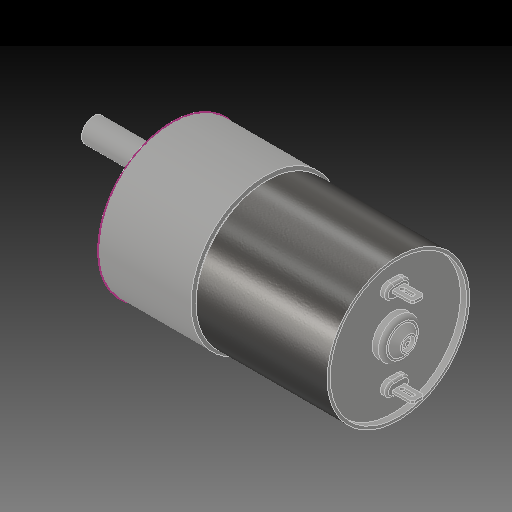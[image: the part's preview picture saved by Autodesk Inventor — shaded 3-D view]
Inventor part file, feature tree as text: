
AUTODESK INVENTOR PART (.ipt)
format: ipt  version: 2020 (Build 240168000, 168)  size: 284,160 bytes
history: native  units: mm
features: sketch x2, projected_geometry x2, extrude x1, other x1
ambient origin geometry x8: Origin, YZ Plane, XZ Plane, XY Plane, X Axis, Y Axis, Z Axis, Center Point
bodies: Solid1 (feature_tree)
feature tree (6):
  sketch  "Sketch1"  dims[d0=8.0mm d1=45.75mm d2=0.0mm]
  extrude  "Extrusion1"  Depth=45.75mm TaperAngle=0.0deg
  projected_geometry  "Projected Loop1"
  projected_geometry  "Projected Loop2"
  sketch  "Sketch2"
  other  "Aynalama2"
